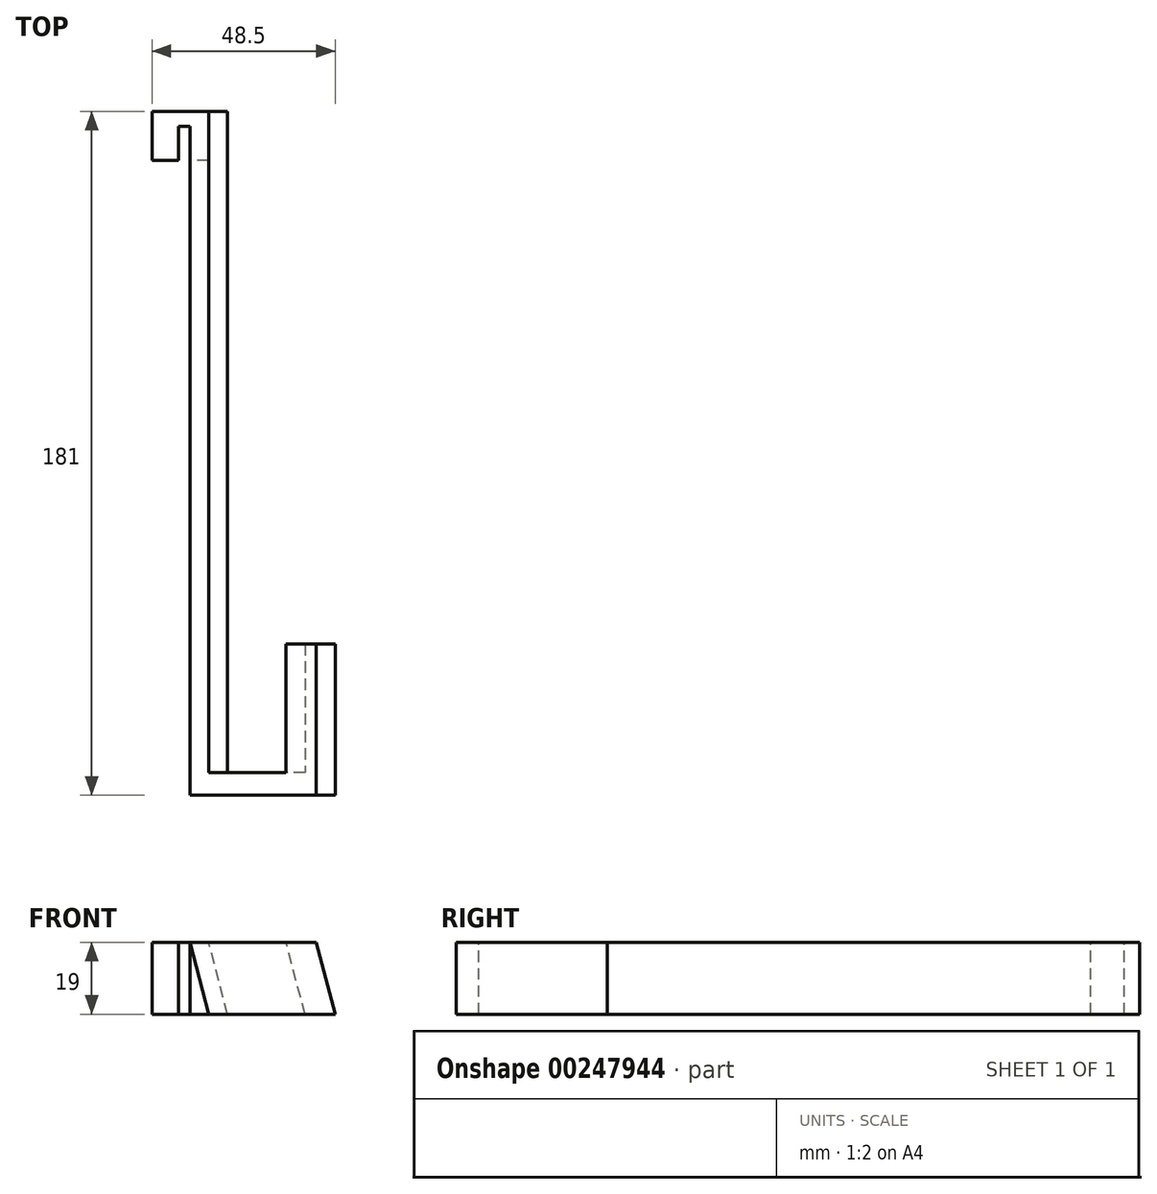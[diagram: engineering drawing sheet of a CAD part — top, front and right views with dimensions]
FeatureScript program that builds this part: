
annotation { "Feature Type Name" : "Feature", "Feature Type Description" : "" }
export const myFeature = defineFeature(function(context is Context, id is Id, definition is map)
    precondition{}
    {
        {
            var Q0;
            Q0=qCreatedBy(makeId("Top.planeOp"),FACE);
            var sketch = newSketch(context, id + "F0", { "sketchPlane" : qUnion([Q0])});
            skLineSegment(sketch, "E0", {"start": v(-20.88, 29.23) * mm, "end": v(-35.88, 29.23) * mm});
            skLineSegment(sketch, "E1", {"start": v(-35.88, 29.23) * mm, "end": v(-35.88, 42.23) * mm});
            skLineSegment(sketch, "E2", {"start": v(-35.88, 42.23) * mm, "end": v(-15.88, 42.23) * mm});
            skLineSegment(sketch, "E3", {"start": v(-15.88, 42.23) * mm, "end": v(-15.88, -132.77) * mm});
            skLineSegment(sketch, "E4", {"start": v(-20.88, 29.23) * mm, "end": v(-20.88, -138.77) * mm});
            skLineSegment(sketch, "E5", {"start": v(-20.88, -138.77) * mm, "end": v(12.62, -138.77) * mm});
            skLineSegment(sketch, "E6", {"start": v(12.62, -138.77) * mm, "end": v(12.62, -98.77) * mm});
            skLineSegment(sketch, "E7", {"start": v(12.62, -98.77) * mm, "end": v(4.62, -98.77) * mm});
            skLineSegment(sketch, "E8", {"start": v(4.62, -98.77) * mm, "end": v(4.62, -132.77) * mm});
            skLineSegment(sketch, "E9", {"start": v(4.62, -132.77) * mm, "end": v(-15.88, -132.77) * mm});
            skPoint(sketch, "E10.end.orphan", {"position": v(-29.88, 38.23) * mm});
            skPoint(sketch, "E11.orphan", {"position": v(-29.88, 29.23) * mm});
            skSolve(sketch);
        }
        {
            var Q0;
            Q0=qCreatedBy(makeId("Top.planeOp"),FACE);
            cPlane(context, id + "F1", {"entities" : qUnion([Q0]), "cplaneType" : CPlaneType.OFFSET, "offset" : 19 * mm, "width" : 150 * mm, "height" : 150 * mm});
        }
        {
            var Q0;
            Q0=qCreatedBy(id+"F1.planeOp",FACE);
            var sketch = newSketch(context, id + "F2", { "sketchPlane" : qUnion([Q0])});
            skLineSegment(sketch, "E12", {"start": v(-25.88, 29.23) * mm, "end": v(-35.88, 29.23) * mm});
            skLineSegment(sketch, "E13", {"start": v(-35.88, 29.23) * mm, "end": v(-35.88, 42.23) * mm});
            skLineSegment(sketch, "E14", {"start": v(-35.88, 42.23) * mm, "end": v(-20.88, 42.23) * mm});
            skLineSegment(sketch, "E15", {"start": v(-20.88, 42.23) * mm, "end": v(-20.88, -132.77) * mm});
            skLineSegment(sketch, "E16", {"start": v(-25.88, 29.23) * mm, "end": v(-25.88, -138.77) * mm});
            skLineSegment(sketch, "E17", {"start": v(-25.88, -138.77) * mm, "end": v(7.62, -138.77) * mm});
            skLineSegment(sketch, "E18", {"start": v(7.62, -138.77) * mm, "end": v(7.62, -98.77) * mm});
            skLineSegment(sketch, "E19", {"start": v(7.62, -98.77) * mm, "end": v(-0.38, -98.77) * mm});
            skLineSegment(sketch, "E20", {"start": v(-0.38, -98.77) * mm, "end": v(-0.38, -132.77) * mm});
            skLineSegment(sketch, "E21", {"start": v(-0.38, -132.77) * mm, "end": v(-20.88, -132.77) * mm});
            skPoint(sketch, "E22.end.orphan", {"position": v(-34.88, 38.23) * mm});
            skPoint(sketch, "E23.orphan", {"position": v(-34.88, 29.23) * mm});
            skSolve(sketch);
        }
        {
            var Q0;
            Q0 = qSketchRegion(id + "F0", true);
            var Q1;
            Q1=makeQuery(id+"F2.imprint","IMPRINT",FACE,{"disambiguationData":[TD([[makeQuery(id+"F2.imprint","IMPRINT",EDGE,{"derivedFrom":sQuery(id+"F2.wireOp",EDGE,"E12")}),-1.0]])]});
            loft(context, id + "F3", {"sheetProfilesArray" : [{ "sheetProfileEntities" : qUnion([Q0]) }, { "sheetProfileEntities" : qUnion([Q1]) }]});
        }
        {
            var Q0;
            Q0=makeQuery(id+"F3.opLoft","CAP_FACE",FACE,{"disambiguationData":[OSD([makeQuery(id+"F2.imprint","IMPRINT",FACE,{"disambiguationData":[TD([[makeQuery(id+"F2.imprint","IMPRINT",EDGE,{"derivedFrom":sQuery(id+"F2.wireOp",EDGE,"E12")}),-1.0]])]})])],"isStart":true});
            var sketch = newSketch(context, id + "F4", { "sketchPlane" : qUnion([Q0])});
            skLineSegment(sketch, "E24.bottom", {"start": v(-25.88, 29.23) * mm, "end": v(-28.88, 29.23) * mm});
            skLineSegment(sketch, "E24.top", {"start": v(-25.88, 38.23) * mm, "end": v(-28.88, 38.23) * mm});
            skLineSegment(sketch, "E24.left", {"start": v(-25.88, 29.23) * mm, "end": v(-25.88, 38.23) * mm});
            skLineSegment(sketch, "E24.right", {"start": v(-28.88, 29.23) * mm, "end": v(-28.88, 38.23) * mm});
            skSolve(sketch);
        }
        {
            var Q0;
            Q0=makeQuery(id+"F4.imprint","IMPRINT",FACE,{"disambiguationData":[TD([[makeQuery(id+"F4.imprint","IMPRINT",EDGE,{"derivedFrom":sQuery(id+"F4.wireOp",EDGE,"E24.bottom")}),1.0]])]});
            extrude(context, id + "F5", {"entities" : qUnion([Q0]), "operationType" : NewBodyOperationType.REMOVE, "oppositeDirection" : true, "depth" : 25 * mm});
        }
    });
